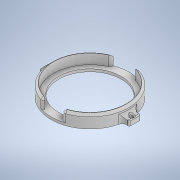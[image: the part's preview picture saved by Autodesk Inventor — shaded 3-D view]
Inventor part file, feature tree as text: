
AUTODESK INVENTOR PART (.ipt)
format: ipt  version: 2022 (Build 260153000, 153)  size: 271,360 bytes
history: native  units: in
note: dims shown in document units (in); Inventor stores cm internally (conversion verified against a paired STEP export)
features: sketch x7, extrude x5, fillet x3, pattern_circular x2, chamfer x2, revolve x1, hole x1
ambient origin geometry x8: Origin, YZ Plane, XZ Plane, XY Plane, X Axis, Y Axis, Z Axis, Center Point
bodies: Solid1 (feature_tree)
feature tree (21):
  extrude  "Extrusion1"  Depth=0.3937in TaperAngle=0.0deg
  extrude  "Extrusion2"  Depth=0.315in TaperAngle=0.0deg
  extrude  "Extrusion3"  Depth=0.0787in TaperAngle=0.0deg
  extrude  "Extrusion4"  Depth=0.6299in
  pattern_circular  "Circular Pattern1"  Count=2 Angle=360.0deg
  fillet  "Fillet1"  Radius=0.0787in
  chamfer  "Chamfer3"  Distance=0.0669in Angle=45.0deg
  extrude  "Extrusion6"  Depth=0.0984in
  revolve  "Revolution2"  [1 undecoded]
  fillet  "Fillet9"  Radius=1.1479in
  fillet  "Fillet10"  Radius=2.5591in
  hole  "Hole2"  [1 undecoded]
  chamfer  "Chamfer5"  Distance=0.1378in
  pattern_circular  "Circular Pattern3"  Angle=15.0deg  [1 undecoded]
  sketch  "Sketch1"  dims[d0=2.4252in d1=0.3937in d2=0.0in]
  sketch  "Sketch2"  dims[d3=2.2677in d4=0.315in d5=0.0in]
  sketch  "Sketch3"  dims[d6=1.9528in d7=0.0787in d8=0.0in]
  sketch  "Sketch4"  dims[d9=0.0in d10=0.6299in]
  sketch  "Sketch7"  dims[d11=60.0deg]
  sketch  "Sketch8"  dims[d12=120.0deg]
  sketch  "Sketch9"  dims[d13=0.3937in d14=0.0in d15=0.7874in d16=360.0deg d18=0.0787in d54=0.0669in d55=0.0787in d56=45.0deg d57=0.0984in d58=0.0984in d59=1.1479in d60=2.5591in d61=0.0in d65=0.1969in d66=0.1378in d67=15.0deg d68=0.1378in d69=0.0394in d70=1.2992in d71=0.0984in d72=0.2362in d73=0.1575in d74=0.0787in d75=90.0deg d76=0.315in d77=0.8108in d78=0.0315in d79=0.0787in d80=45.0deg d81=0.7874in d82=360.0deg]
note: 3 required parameter values undecoded (feature->parameter linkage not recoverable at this tier; creation-order binding heuristic only, values carry confidence <= 0.55)